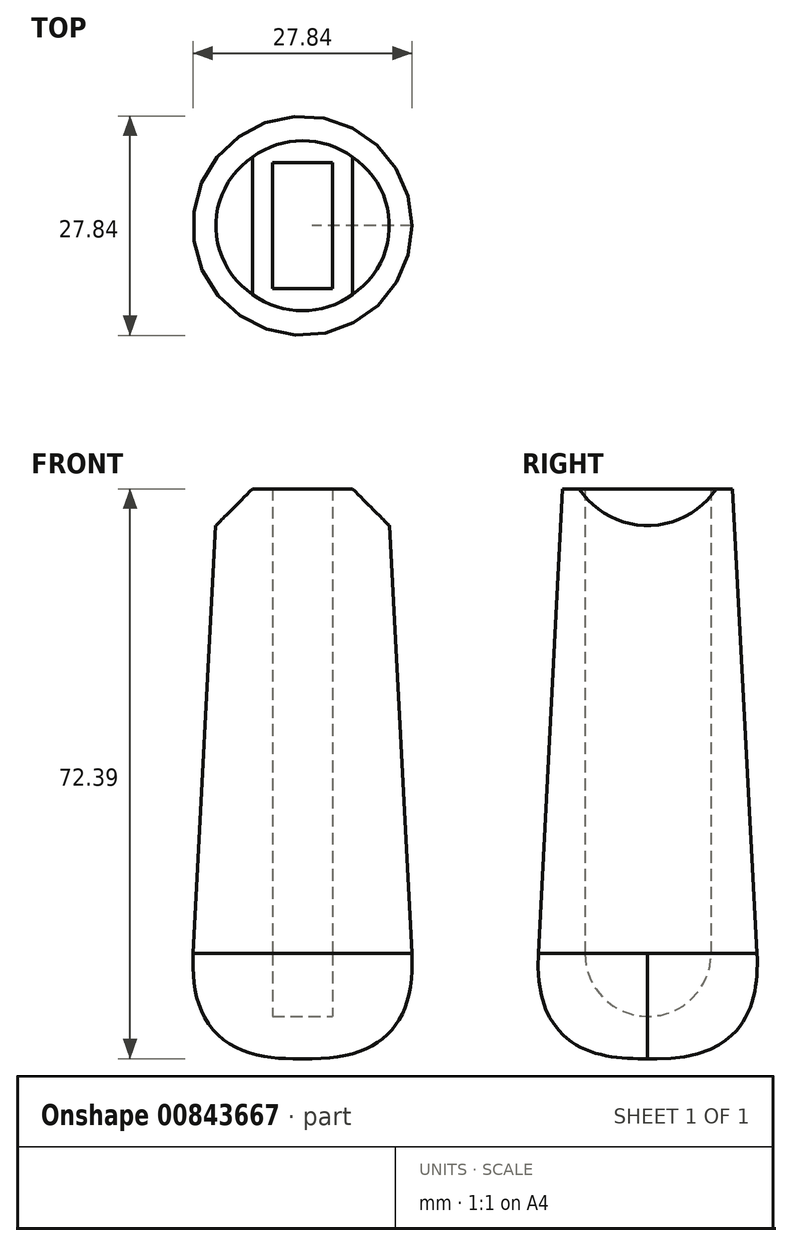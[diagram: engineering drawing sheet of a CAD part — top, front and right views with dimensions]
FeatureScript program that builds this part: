
annotation { "Feature Type Name" : "Feature", "Feature Type Description" : "" }
export const myFeature = defineFeature(function(context is Context, id is Id, definition is map)
    precondition{}
    {
        {
            var Q0;
            Q0=qCreatedBy(makeId("Top.planeOp"),FACE);
            var sketch = newSketch(context, id + "F0", { "sketchPlane" : qUnion([Q0])});
            skCircle(sketch, "E0", {"center": v(0, 0) * mm, "radius": 10.8 * mm});
            skSolve(sketch);
        }
        {
            var Q0;
            Q0=makeQuery(id+"F0.imprint","IMPRINT",FACE,{"disambiguationData":[TD([[makeQuery(id+"F0.imprint","IMPRINT",EDGE,{"derivedFrom":sQuery(id+"F0.wireOp",EDGE,"E0")}),1.0]])]});
            extrude(context, id + "F1", {"entities" : qUnion([Q0]), "oppositeDirection" : true, "depth" : 144.78 * mm / 2, "offsetDistance" : 25.4 * mm, "hasDraft" : true, "draftAngle" : 3 * degree});
        }
        {
            var Q0;
            Q0=makeQuery(id+"F1.opExtrude","CAP_FACE",FACE,{"disambiguationData":[OSD([sQuery(id+"F0.wireOp",EDGE,"E0")])],"isStart":false});
            fillet(context, id + "F2", {"entities" : qUnion([Q0]), "radius" : 25.4 * mm / 2, "tangentPropagation" : true, "rho" : 0.5, "crossSection" : FilletCrossSection.CONIC, "allowEdgeOverflow" : false});
        }
        {
            var Q0;
            Q0=qCreatedBy(makeId("Right.planeOp"),FACE);
            var sketch = newSketch(context, id + "F3", { "sketchPlane" : qUnion([Q0])});
            skLineSegment(sketch, "E1.bottom", {"start": v(-7.96, 0) * mm, "end": v(8.05, 0) * mm});
            skLineSegment(sketch, "E1.left", {"start": v(-7.96, 0) * mm, "end": v(-7.96, -59.03) * mm});
            skLineSegment(sketch, "E1.right", {"start": v(8.05, 0) * mm, "end": v(8.05, -59.03) * mm});
            skArc(sketch, "E2", {"start": v(-7.96, -59.03) * mm, "mid": v(0.05, -67.03) * mm, "end": v(8.05, -59.03) * mm});
            skSolve(sketch);
        }
        {
            var Q0;
            Q0 = qSketchRegion(id + "F3", true);
            extrude(context, id + "F4", {"entities" : qUnion([Q0]), "operationType" : NewBodyOperationType.REMOVE, "oppositeDirection" : true, "depth" : 7.62 * mm / 2, "offsetDistance" : 25.4 * mm, "hasSecondDirection" : true, "secondDirectionOppositeDirection" : false, "secondDirectionDepth" : 7.62 * mm / 2});
        }
        {
            var Q0;
            Q0=qCreatedBy(makeId("Front.planeOp"),FACE);
            var sketch = newSketch(context, id + "F5", { "sketchPlane" : qUnion([Q0])});
            skLineSegment(sketch, "E3", {"start": v(-6.35, 0) * mm, "end": v(6.35, 0) * mm});
            skLineSegment(sketch, "E4", {"start": v(6.35, 0) * mm, "end": v(12.7, -6.35) * mm});
            skLineSegment(sketch, "E5", {"start": v(12.7, -6.35) * mm, "end": v(12.7, 6.35) * mm});
            skLineSegment(sketch, "E6", {"start": v(12.7, 6.35) * mm, "end": v(-12.7, 6.35) * mm});
            skLineSegment(sketch, "E7", {"start": v(-12.7, 6.35) * mm, "end": v(-12.7, -6.35) * mm});
            skLineSegment(sketch, "E8", {"start": v(-12.7, -6.35) * mm, "end": v(-6.35, 0) * mm});
            skPoint(sketch, "E9", {"position": v(0, 0) * mm});
            skSolve(sketch);
        }
        {
            var Q0;
            Q0=makeQuery(id+"F5.imprint","IMPRINT",FACE,{"disambiguationData":[TD([[makeQuery(id+"F5.imprint","IMPRINT",EDGE,{"derivedFrom":sQuery(id+"F5.wireOp",EDGE,"E3")}),1.0]])]});
            extrude(context, id + "F6", {"entities" : qUnion([Q0]), "operationType" : NewBodyOperationType.REMOVE, "oppositeDirection" : true, "depth" : 76.2 * mm / 2, "offsetDistance" : 25.4 * mm, "hasSecondDirection" : true, "secondDirectionOppositeDirection" : false, "secondDirectionDepth" : 25.4 * mm / 2});
        }
    });
